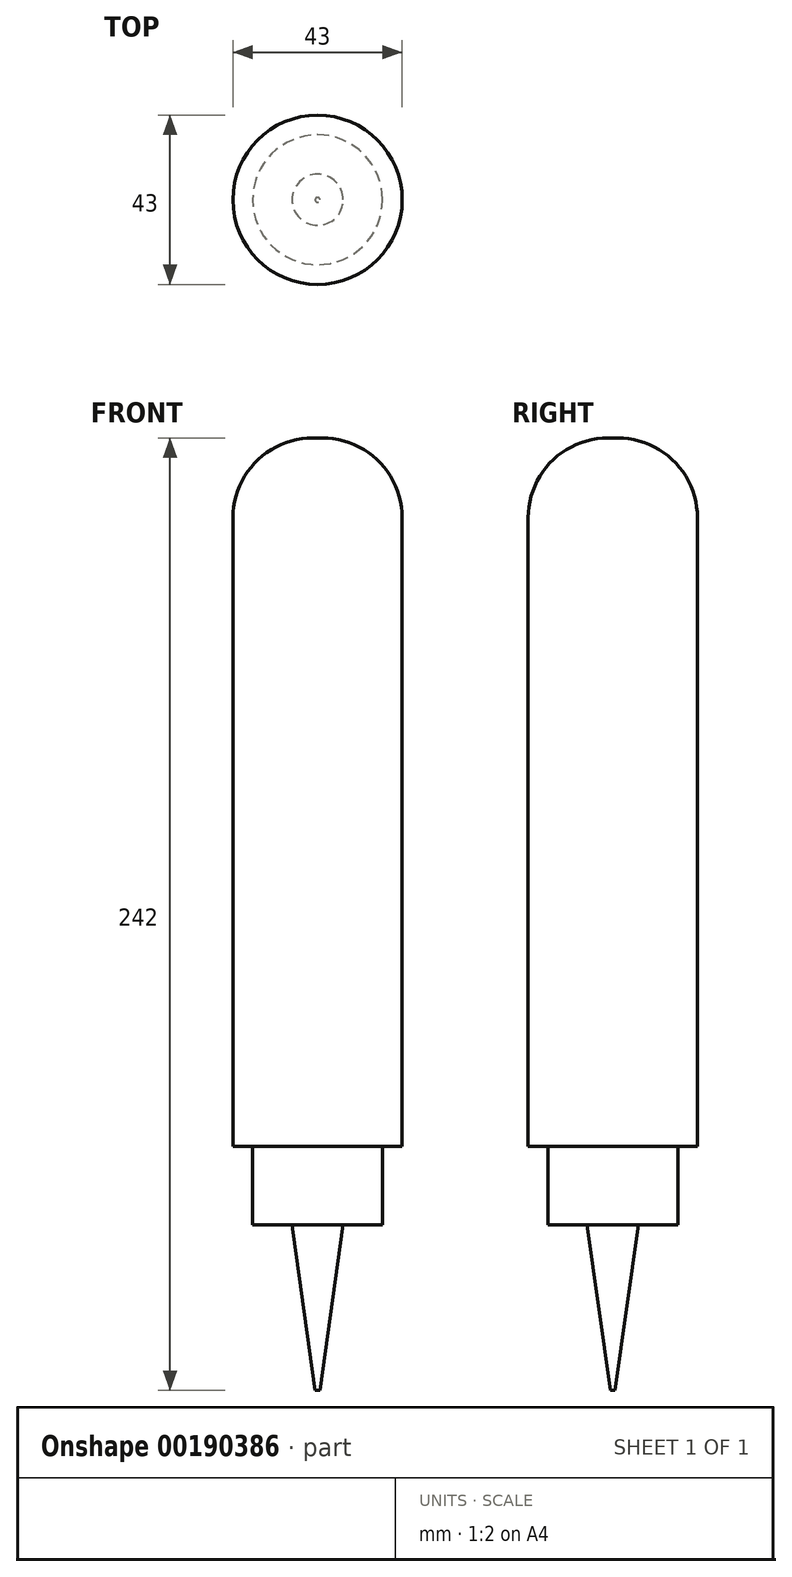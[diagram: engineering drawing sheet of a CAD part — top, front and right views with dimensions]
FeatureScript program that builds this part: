
annotation { "Feature Type Name" : "Feature", "Feature Type Description" : "" }
export const myFeature = defineFeature(function(context is Context, id is Id, definition is map)
    precondition{}
    {
        {
            var Q0;
            Q0=qCreatedBy(makeId("Top.planeOp"),FACE);
            var sketch = newSketch(context, id + "F0", { "sketchPlane" : qUnion([Q0])});
            skCircle(sketch, "E0", {"center": v(27.26, 24.68) * mm, "radius": 21.5 * mm});
            skCircle(sketch, "E1", {"center": v(27.26, 24.68) * mm, "radius": 16.5 * mm});
            skSolve(sketch);
        }
        {
            var Q0;
            Q0=makeQuery(id+"F0.imprint","IMPRINT",FACE,{"disambiguationData":[TD([[makeQuery(id+"F0.imprint","IMPRINT",EDGE,{"derivedFrom":sQuery(id+"F0.wireOp",EDGE,"E0")}),1.0]])]});
            var Q1;
            Q1=makeQuery(id+"F0.imprint","IMPRINT",FACE,{"disambiguationData":[TD([[makeQuery(id+"F0.imprint","IMPRINT",EDGE,{"derivedFrom":sQuery(id+"F0.wireOp",EDGE,"E1")}),1.0]])]});
            extrude(context, id + "F1", {"entities" : qUnion([Q0, Q1]), "depth" : 250 * mm, "hasSecondDirection" : true, "secondDirectionOppositeDirection" : false, "secondDirectionDepth" : 50 * mm});
        }
        {
            var Q0;
            Q0=makeQuery(id+"F0.imprint","IMPRINT",FACE,{"disambiguationData":[TD([[makeQuery(id+"F0.imprint","IMPRINT",EDGE,{"derivedFrom":sQuery(id+"F0.wireOp",EDGE,"E0")}),1.0]])]});
            extrude(context, id + "F2", {"entities" : qUnion([Q0]), "operationType" : NewBodyOperationType.REMOVE, "depth" : 70 * mm});
        }
        {
            var Q0;
            Q0=makeQuery(id+"F1.opExtrude","CAP_FACE",FACE,{"disambiguationData":[OSD([sQuery(id+"F0.wireOp",EDGE,"E0")])],"isStart":true});
            var sketch = newSketch(context, id + "F3", { "sketchPlane" : qUnion([Q0])});
            skCircle(sketch, "E2", {"center": v(27.26, -24.68) * mm, "radius": 6.5 * mm});
            skSolve(sketch);
        }
        {
            var Q0;
            Q0=makeQuery(id+"F3.imprint","IMPRINT",FACE,{"disambiguationData":[TD([[makeQuery(id+"F3.imprint","IMPRINT",EDGE,{"derivedFrom":sQuery(id+"F3.wireOp",EDGE,"E2")}),1.0]])]});
            extrude(context, id + "F4", {"entities" : qUnion([Q0]), "operationType" : NewBodyOperationType.ADD, "depth" : 42 * mm, "hasDraft" : true, "draftAngle" : 8 * degree, "draftPullDirection" : true});
        }
        {
            var Q0;
            Q0=makeQuery(id+"F1.opExtrude","CAP_EDGE",EDGE,{"disambiguationData":[OSD([sQuery(id+"F0.wireOp",EDGE,"E0")])],"isStart":false});
            fillet(context, id + "F5", {"entities" : qUnion([Q0]), "radius" : 20.28 * mm, "tangentPropagation" : true, "allowEdgeOverflow" : false});
        }
    });
